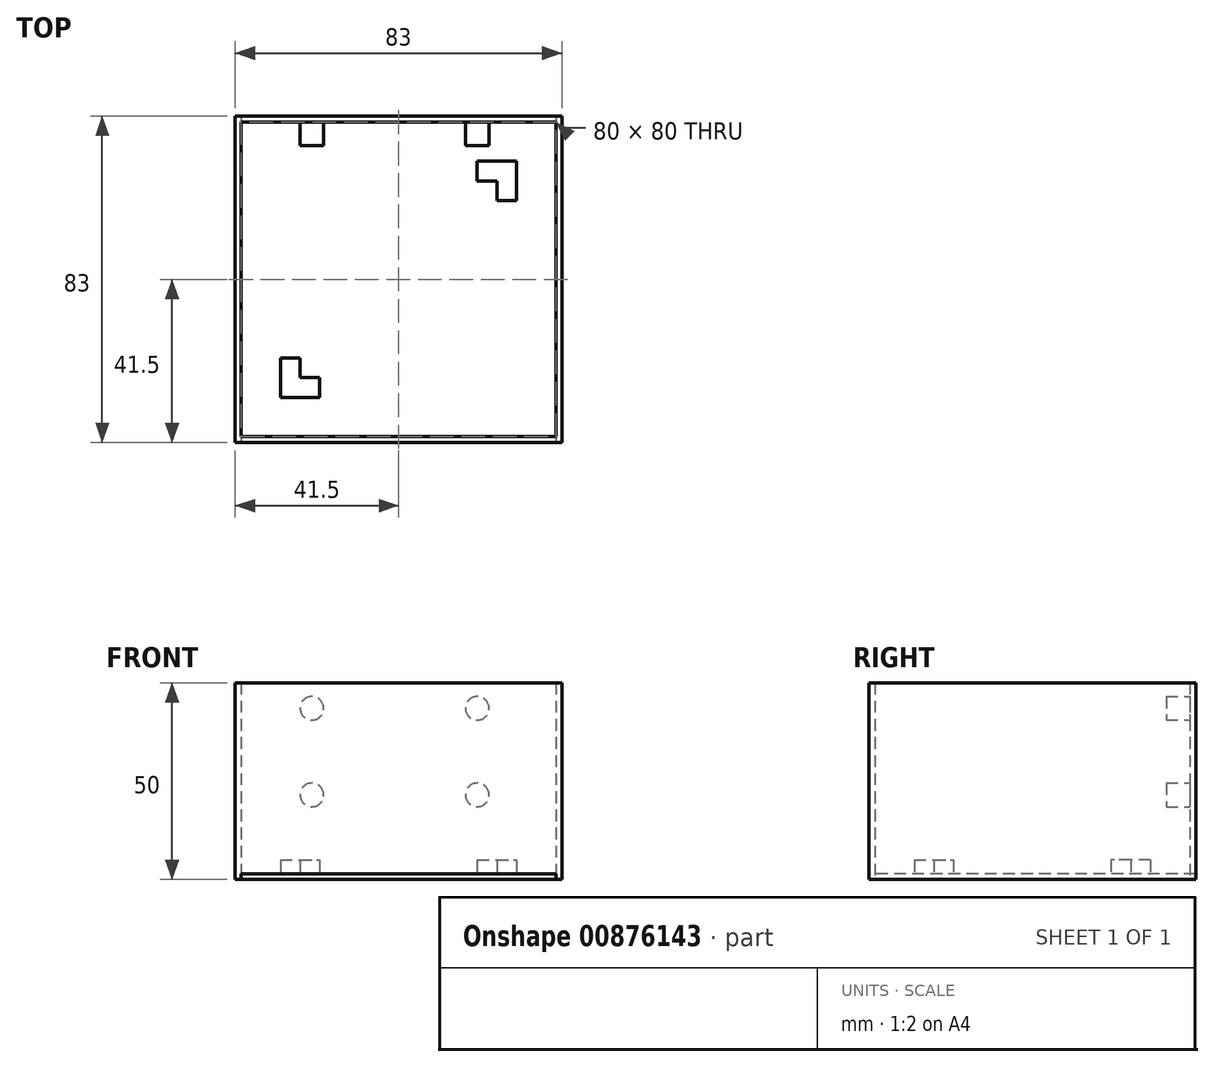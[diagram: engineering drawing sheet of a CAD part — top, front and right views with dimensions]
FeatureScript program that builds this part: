
annotation { "Feature Type Name" : "Feature", "Feature Type Description" : "" }
export const myFeature = defineFeature(function(context is Context, id is Id, definition is map)
    precondition{}
    {
        {
            var Q0;
            Q0=qCreatedBy(makeId("Top.planeOp"),FACE);
            var sketch = newSketch(context, id + "F0", { "sketchPlane" : qUnion([Q0])});
            skLineSegment(sketch, "E0", {"start": v(0, 0) * mm, "end": v(0, 80) * mm});
            skLineSegment(sketch, "E1", {"start": v(0, 80) * mm, "end": v(80, 80) * mm});
            skLineSegment(sketch, "E2", {"start": v(80, 80) * mm, "end": v(80, 0) * mm});
            skLineSegment(sketch, "E3", {"start": v(0, 0) * mm, "end": v(80, 0) * mm});
            skLineSegment(sketch, "E4.0", {"start": v(15, 15) * mm, "end": v(20, 15) * mm});
            skLineSegment(sketch, "E5.0", {"start": v(15, 15) * mm, "end": v(15, 20) * mm});
            skLineSegment(sketch, "E6.0", {"start": v(60, 65) * mm, "end": v(65, 65) * mm});
            skLineSegment(sketch, "E7.0", {"start": v(65, 65) * mm, "end": v(65, 60) * mm});
            skLineSegment(sketch, "E8.0", {"start": v(10, 10) * mm, "end": v(10, 20) * mm});
            skLineSegment(sketch, "E9.1", {"start": v(70, 70) * mm, "end": v(70, 60) * mm});
            skLineSegment(sketch, "E9.2", {"start": v(10, 10) * mm, "end": v(20, 10) * mm});
            skLineSegment(sketch, "E10.0", {"start": v(60, 70) * mm, "end": v(60, 65) * mm});
            skLineSegment(sketch, "E11.trimOffspring", {"start": v(60, 70) * mm, "end": v(70, 70) * mm});
            skLineSegment(sketch, "E12.trimOffspring", {"start": v(65, 60) * mm, "end": v(70, 60) * mm});
            skLineSegment(sketch, "E13.0", {"start": v(20, 10) * mm, "end": v(20, 15) * mm});
            skLineSegment(sketch, "E14.0", {"start": v(10, 20) * mm, "end": v(15, 20) * mm});
            skLineSegment(sketch, "E15.0", {"start": v(-1.5, -1.5) * mm, "end": v(-1.5, 81.5) * mm});
            skLineSegment(sketch, "E16.0", {"start": v(-1.5, 81.5) * mm, "end": v(81.5, 81.5) * mm});
            skLineSegment(sketch, "E17.0", {"start": v(81.5, 81.5) * mm, "end": v(81.5, -1.5) * mm});
            skLineSegment(sketch, "E18.0", {"start": v(-1.5, -1.5) * mm, "end": v(81.5, -1.5) * mm});
            skSolve(sketch);
        }
        {
            var Q0;
            Q0=makeQuery(id+"F0.imprint","IMPRINT",FACE,{"disambiguationData":[TD([[makeQuery(id+"F0.imprint","IMPRINT",EDGE,{"derivedFrom":sQuery(id+"F0.wireOp",EDGE,"E4.0")}),-1.0]])]});
            var Q1;
            Q1=makeQuery(id+"F0.imprint","IMPRINT",FACE,{"disambiguationData":[TD([[makeQuery(id+"F0.imprint","IMPRINT",EDGE,{"derivedFrom":sQuery(id+"F0.wireOp",EDGE,"E6.0")}),1.0]])]});
            extrude(context, id + "F1", {"entities" : qUnion([Q0, Q1]), "depth" : 5 * mm, "offsetDistance" : 25 * mm});
        }
        {
            var Q0;
            Q0 = qSketchRegion(id + "F0", true);
            extrude(context, id + "F2", {"entities" : qUnion([Q0]), "depth" : 50 * mm, "offsetDistance" : 25 * mm});
        }
        {
            var Q0;
            Q0=makeQuery(id+"F2.opExtrude","SWEPT_FACE",FACE,{"disambiguationData":[OSD([sQuery(id+"F0.wireOp",EDGE,"E18.0")])]});
            var sketch = newSketch(context, id + "F3", { "sketchPlane" : qUnion([Q0])});
            skLineSegment(sketch, "E19", {"start": v(0, 0) * mm, "end": v(80, 0) * mm});
            skLineSegment(sketch, "E20.0", {"start": v(0, 1.5) * mm, "end": v(80, 1.5) * mm});
            skLineSegment(sketch, "E21", {"start": v(0, 1.5) * mm, "end": v(0, 0) * mm});
            skLineSegment(sketch, "E22", {"start": v(80, 1.5) * mm, "end": v(80, 0) * mm});
            skSolve(sketch);
        }
        {
            var Q0;
            Q0=makeQuery(id+"F3.imprint","IMPRINT",FACE,{"disambiguationData":[TD([[makeQuery(id+"F3.imprint","IMPRINT",EDGE,{"derivedFrom":sQuery(id+"F3.wireOp",EDGE,"E19")}),1.0]])]});
            extrude(context, id + "F4", {"entities" : qUnion([Q0]), "oppositeDirection" : true, "depth" : 83 * mm, "offsetDistance" : 25 * mm});
        }
        {
            var Q0;
            Q0=makeQuery(id+"F2.opExtrude","SWEPT_FACE",FACE,{"disambiguationData":[OSD([sQuery(id+"F0.wireOp",EDGE,"E1")])]});
            var sketch = newSketch(context, id + "F5", { "sketchPlane" : qUnion([Q0])});
            skCircle(sketch, "E23", {"center": v(18, 43.5) * mm, "radius": 3 * mm});
            skCircle(sketch, "E24", {"center": v(60, 43.5) * mm, "radius": 3 * mm});
            skCircle(sketch, "E25", {"center": v(18, 21.5) * mm, "radius": 3 * mm});
            skCircle(sketch, "E26", {"center": v(60, 21.5) * mm, "radius": 3 * mm});
            skSolve(sketch);
        }
        {
            var Q0;
            Q0 = qSketchRegion(id + "F5", true);
            extrude(context, id + "F6", {"entities" : qUnion([Q0]), "operationType" : NewBodyOperationType.ADD, "depth" : 6 * mm, "offsetDistance" : 25 * mm});
        }
    });
